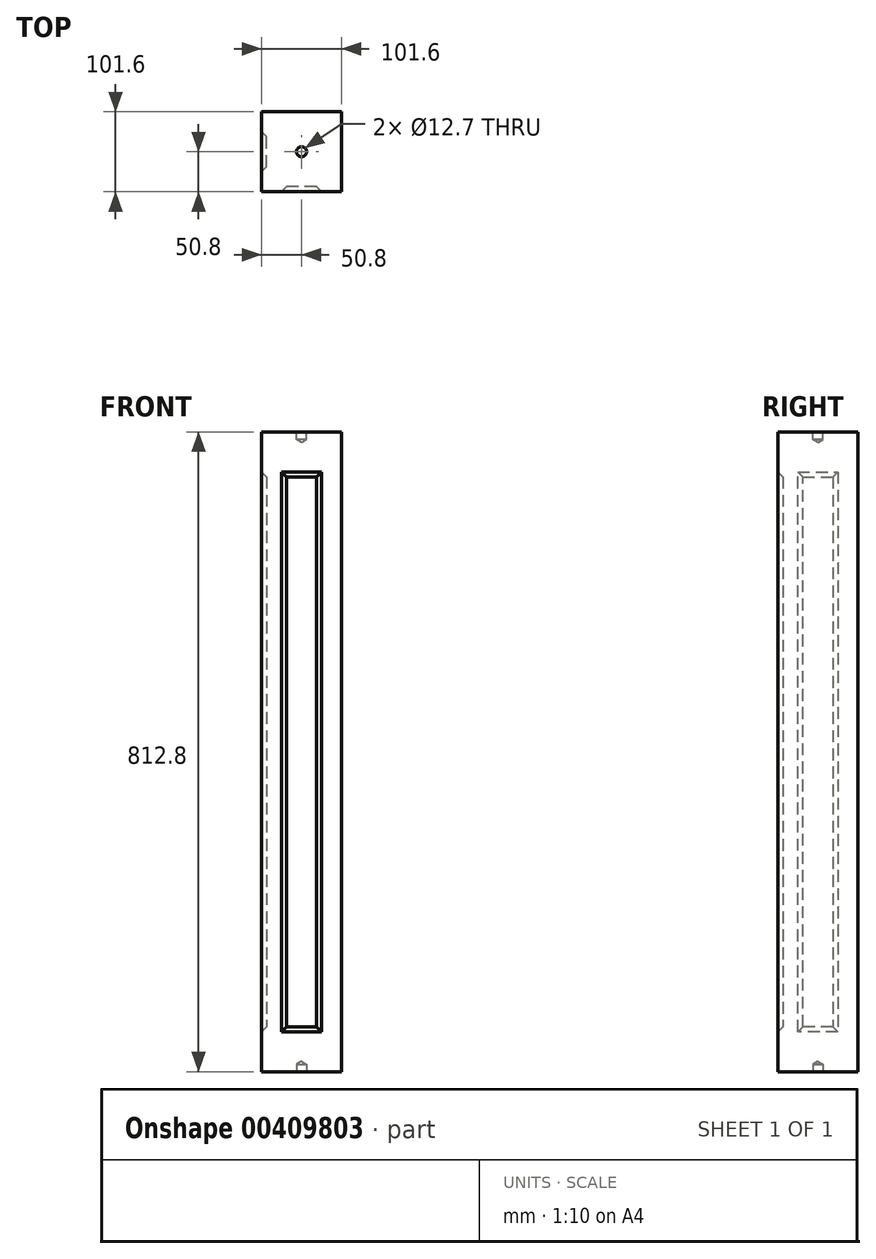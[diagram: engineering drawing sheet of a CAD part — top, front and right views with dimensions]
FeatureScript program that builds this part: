
annotation { "Feature Type Name" : "Feature", "Feature Type Description" : "" }
export const myFeature = defineFeature(function(context is Context, id is Id, definition is map)
    precondition{}
    {
        {
            var Q0;
            Q0=qCreatedBy(makeId("Front.planeOp"),FACE);
            var sketch = newSketch(context, id + "F0", { "sketchPlane" : qUnion([Q0])});
            skLineSegment(sketch, "E0.bottom", {"start": v(-50.8, 406.4) * mm, "end": v(50.8, 406.4) * mm});
            skLineSegment(sketch, "E0.top", {"start": v(-50.8, -406.4) * mm, "end": v(50.8, -406.4) * mm});
            skLineSegment(sketch, "E0.left", {"start": v(-50.8, 406.4) * mm, "end": v(-50.8, -406.4) * mm});
            skLineSegment(sketch, "E0.right", {"start": v(50.8, 406.4) * mm, "end": v(50.8, -406.4) * mm});
            skPoint(sketch, "E0.middle", {"position": v(0, 0) * mm});
            skSolve(sketch);
        }
        {
            var Q0;
            Q0=makeQuery(id+"F0.imprint","IMPRINT",FACE,{"disambiguationData":[TD([[makeQuery(id+"F0.imprint","IMPRINT",EDGE,{"derivedFrom":sQuery(id+"F0.wireOp",EDGE,"E0.bottom")}),-1.0]])]});
            extrude(context, id + "F1", {"entities" : qUnion([Q0]), "endBound" : BoundingType.SYMMETRIC, "depth" : 101.6 * mm});
        }
        {
            var Q0;
            Q0=makeQuery(id+"F1.opExtrude","SWEPT_FACE",FACE,{"disambiguationData":[OSD([sQuery(id+"F0.wireOp",EDGE,"E0.bottom")])]});
            var sketch = newSketch(context, id + "F2", { "sketchPlane" : qUnion([Q0])});
            skPoint(sketch, "E1", {"position": v(0, 0) * mm});
            skCircle(sketch, "E2", {"center": v(0, 0) * mm, "radius": 6.35 * mm});
            skSolve(sketch);
        }
        {
            var Q0;
            Q0=sQuery(id+"F2.wireOp",VERTEX,"E1");
            var Q1;
            Q1=makeQuery(id+"F1.opExtrude","SWEPT_BODY",BODY,{"disambiguationData":[OSD([sQuery(id+"F0.wireOp",EDGE,"E0.bottom"),sQuery(id+"F0.wireOp",EDGE,"E0.top"),sQuery(id+"F0.wireOp",EDGE,"E0.left"),sQuery(id+"F0.wireOp",EDGE,"E0.right")])]});
            hole(context, id + "F3", {"style" : HoleStyle.SIMPLE, "endStyle" : HoleEndStyle.BLIND, "holeDiameter" : 12.7 * mm, "holeDepth" : 9.52 * mm, "isTappedThrough" : true, "tappedDepth" : 12.7 * mm, "tapClearance" : 3, "locations" : qUnion([Q0]), "scope" : qUnion([Q1])});
        }
        {
            var Q0;
            Q0=makeQuery(id+"F1.opExtrude","SWEPT_FACE",FACE,{"disambiguationData":[OSD([sQuery(id+"F0.wireOp",EDGE,"E0.top")])]});
            var sketch = newSketch(context, id + "F4", { "sketchPlane" : qUnion([Q0])});
            skCircle(sketch, "E3", {"center": v(0, 0) * mm, "radius": 6.35 * mm});
            skSolve(sketch);
        }
        {
            var Q0;
            Q0=sQuery(id+"F4.wireOp",VERTEX,"E3.center");
            var Q1;
            Q1=makeQuery(id+"F1.opExtrude","SWEPT_BODY",BODY,{"disambiguationData":[OSD([sQuery(id+"F0.wireOp",EDGE,"E0.bottom"),sQuery(id+"F0.wireOp",EDGE,"E0.top"),sQuery(id+"F0.wireOp",EDGE,"E0.left"),sQuery(id+"F0.wireOp",EDGE,"E0.right")])]});
            hole(context, id + "F5", {"style" : HoleStyle.SIMPLE, "endStyle" : HoleEndStyle.BLIND, "holeDiameter" : 12.7 * mm, "holeDepth" : 9.52 * mm, "isTappedThrough" : true, "tappedDepth" : 12.7 * mm, "tapClearance" : 3, "locations" : qUnion([Q0]), "scope" : qUnion([Q1])});
        }
        {
            var Q0;
            Q0=makeQuery(id+"F1.opExtrude","CAP_FACE",FACE,{"disambiguationData":[OSD([sQuery(id+"F0.wireOp",EDGE,"E0.bottom"),sQuery(id+"F0.wireOp",EDGE,"E0.top"),sQuery(id+"F0.wireOp",EDGE,"E0.left"),sQuery(id+"F0.wireOp",EDGE,"E0.right")])],"isStart":false});
            var sketch = newSketch(context, id + "F6", { "sketchPlane" : qUnion([Q0])});
            skLineSegment(sketch, "E4.bottom", {"start": v(-25.4, 355.6) * mm, "end": v(25.4, 355.6) * mm});
            skLineSegment(sketch, "E4.top", {"start": v(-25.4, -355.6) * mm, "end": v(25.4, -355.6) * mm});
            skLineSegment(sketch, "E4.left", {"start": v(-25.4, 355.6) * mm, "end": v(-25.4, -355.6) * mm});
            skLineSegment(sketch, "E4.right", {"start": v(25.4, 355.6) * mm, "end": v(25.4, -355.6) * mm});
            skPoint(sketch, "E4.middle", {"position": v(0, 0) * mm});
            skSolve(sketch);
        }
        {
            var Q0;
            Q0=makeQuery(id+"F1.opExtrude","SWEPT_FACE",FACE,{"disambiguationData":[OSD([sQuery(id+"F0.wireOp",EDGE,"E0.left")])]});
            var sketch = newSketch(context, id + "F7", { "sketchPlane" : qUnion([Q0])});
            skLineSegment(sketch, "E5.bottom", {"start": v(-25.4, 355.6) * mm, "end": v(25.4, 355.6) * mm});
            skLineSegment(sketch, "E5.top", {"start": v(-25.4, -355.6) * mm, "end": v(25.4, -355.6) * mm});
            skLineSegment(sketch, "E5.left", {"start": v(-25.4, 355.6) * mm, "end": v(-25.4, -355.6) * mm});
            skLineSegment(sketch, "E5.right", {"start": v(25.4, 355.6) * mm, "end": v(25.4, -355.6) * mm});
            skPoint(sketch, "E5.middle", {"position": v(0, 0) * mm});
            skSolve(sketch);
        }
        {
            var Q0;
            Q0=makeQuery(id+"F6.imprint","IMPRINT",FACE,{"disambiguationData":[TD([[makeQuery(id+"F6.imprint","IMPRINT",EDGE,{"derivedFrom":sQuery(id+"F6.wireOp",EDGE,"E4.bottom")}),-1.0]])]});
            extrude(context, id + "F8", {"entities" : qUnion([Q0]), "operationType" : NewBodyOperationType.REMOVE, "oppositeDirection" : true, "depth" : 6.35 * mm, "hasDraft" : true, "draftAngle" : 45 * degree, "draftPullDirection" : true});
        }
        {
            var Q0;
            Q0=makeQuery(id+"F7.imprint","IMPRINT",FACE,{"disambiguationData":[TD([[makeQuery(id+"F7.imprint","IMPRINT",EDGE,{"derivedFrom":sQuery(id+"F7.wireOp",EDGE,"E5.bottom")}),-1.0]])]});
            extrude(context, id + "F9", {"entities" : qUnion([Q0]), "operationType" : NewBodyOperationType.REMOVE, "oppositeDirection" : true, "depth" : 6.35 * mm, "hasDraft" : true, "draftAngle" : 45 * degree, "draftPullDirection" : true});
        }
    });
